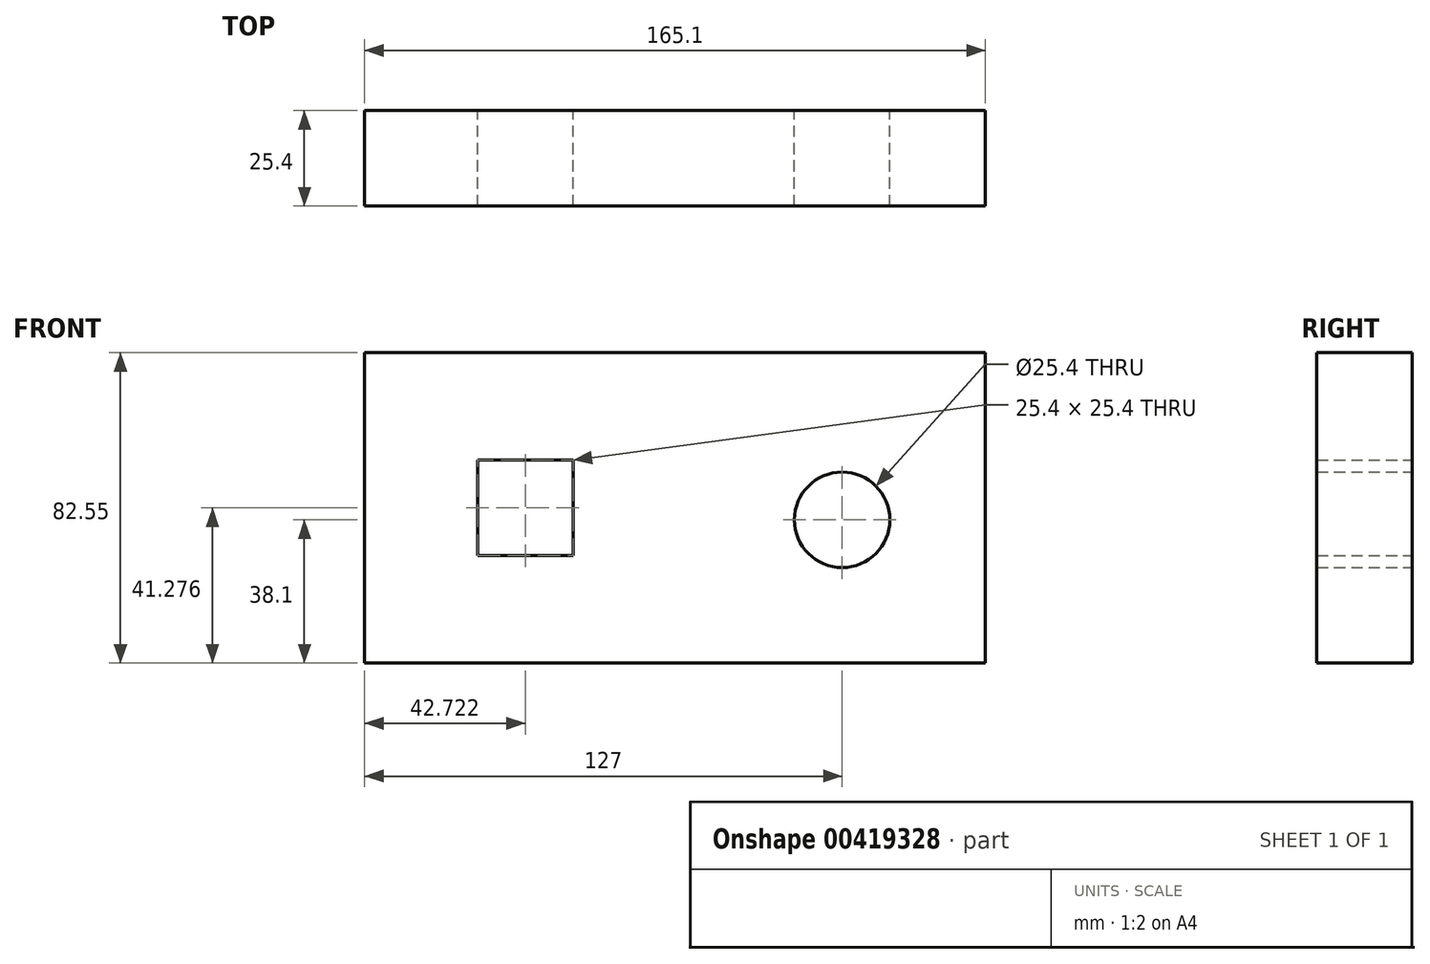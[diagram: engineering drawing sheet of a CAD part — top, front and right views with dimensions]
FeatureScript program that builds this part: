
annotation { "Feature Type Name" : "Feature", "Feature Type Description" : "" }
export const myFeature = defineFeature(function(context is Context, id is Id, definition is map)
    precondition{}
    {
        {
            var Q0;
            Q0=qCreatedBy(makeId("Front.planeOp"),FACE);
            var sketch = newSketch(context, id + "F0", { "sketchPlane" : qUnion([Q0])});
            skLineSegment(sketch, "E0", {"start": v(0, 0) * mm, "end": v(-165.1, 0) * mm});
            skLineSegment(sketch, "E1", {"start": v(-165.1, 0) * mm, "end": v(-165.1, 82.55) * mm});
            skLineSegment(sketch, "E2", {"start": v(-165.1, 82.55) * mm, "end": v(0, 82.55) * mm});
            skLineSegment(sketch, "E3", {"start": v(0, 82.55) * mm, "end": v(0, 0) * mm});
            skSolve(sketch);
        }
        {
            var Q0;
            Q0=makeQuery(id+"F0.imprint","IMPRINT",FACE,{"disambiguationData":[TD([[makeQuery(id+"F0.imprint","IMPRINT",EDGE,{"derivedFrom":sQuery(id+"F0.wireOp",EDGE,"E0")}),-1.0]])]});
            var sketch = newSketch(context, id + "F1", { "sketchPlane" : qUnion([Q0])});
            skLineSegment(sketch, "E4.bottom", {"start": v(-135.08, 53.98) * mm, "end": v(-109.68, 53.98) * mm});
            skLineSegment(sketch, "E4.top", {"start": v(-135.08, 28.58) * mm, "end": v(-109.68, 28.58) * mm});
            skLineSegment(sketch, "E4.left", {"start": v(-135.08, 53.98) * mm, "end": v(-135.08, 28.58) * mm});
            skLineSegment(sketch, "E4.right", {"start": v(-109.68, 53.98) * mm, "end": v(-109.68, 28.58) * mm});
            skSolve(sketch);
        }
        {
            var Q0;
            Q0=makeQuery(id+"F0.imprint","IMPRINT",FACE,{"disambiguationData":[TD([[makeQuery(id+"F0.imprint","IMPRINT",EDGE,{"derivedFrom":sQuery(id+"F0.wireOp",EDGE,"E0")}),-1.0]])]});
            var sketch = newSketch(context, id + "F2", { "sketchPlane" : qUnion([Q0])});
            skCircle(sketch, "E5", {"center": v(-38.1, 38.1) * mm, "radius": 12.7 * mm});
            skSolve(sketch);
        }
        {
            var Q0;
            Q0=makeQuery(id+"F0.imprint","IMPRINT",FACE,{"disambiguationData":[TD([[makeQuery(id+"F0.imprint","IMPRINT",EDGE,{"derivedFrom":sQuery(id+"F0.wireOp",EDGE,"E0")}),-1.0]])]});
            extrude(context, id + "F3", {"entities" : qUnion([Q0]), "depth" : 25.4 * mm});
        }
        {
            var Q0;
            Q0=makeQuery(id+"F1.imprint","IMPRINT",FACE,{"disambiguationData":[TD([[makeQuery(id+"F1.imprint","IMPRINT",EDGE,{"derivedFrom":sQuery(id+"F1.wireOp",EDGE,"E4.bottom")}),-1.0]])]});
            extrude(context, id + "F4", {"entities" : qUnion([Q0]), "operationType" : NewBodyOperationType.REMOVE, "depth" : 812.8 * mm});
        }
        {
            var Q0;
            Q0=makeQuery(id+"F2.imprint","IMPRINT",FACE,{"disambiguationData":[TD([[makeQuery(id+"F2.imprint","IMPRINT",EDGE,{"derivedFrom":sQuery(id+"F2.wireOp",EDGE,"E5")}),1.0]])]});
            extrude(context, id + "F5", {"entities" : qUnion([Q0]), "operationType" : NewBodyOperationType.REMOVE, "depth" : 1752.6 * mm});
        }
    });
